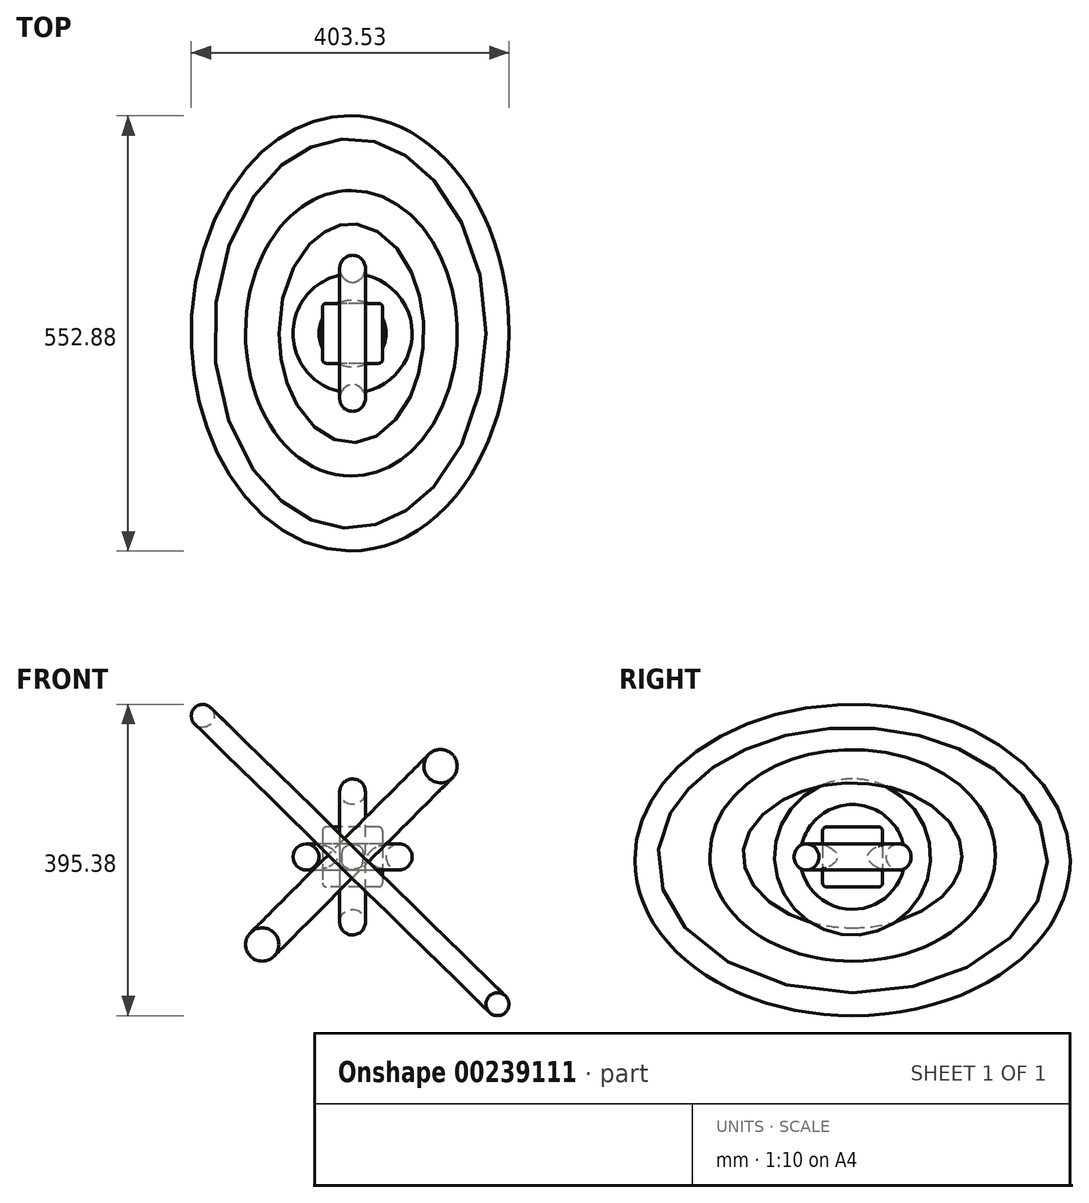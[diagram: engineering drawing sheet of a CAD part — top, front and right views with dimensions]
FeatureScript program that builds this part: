
annotation { "Feature Type Name" : "Feature", "Feature Type Description" : "" }
export const myFeature = defineFeature(function(context is Context, id is Id, definition is map)
    precondition{}
    {
        {
            var Q0;
            Q0=qCreatedBy(makeId("Front.planeOp"),FACE);
            var sketch = newSketch(context, id + "F0", { "sketchPlane" : qUnion([Q0])});
            skLineSegment(sketch, "E0.bottom", {"start": v(38.1, 38.1) * mm, "end": v(-38.1, 38.1) * mm});
            skLineSegment(sketch, "E0.top", {"start": v(38.1, -38.1) * mm, "end": v(-38.1, -38.1) * mm});
            skLineSegment(sketch, "E0.left", {"start": v(38.1, 38.1) * mm, "end": v(38.1, -38.1) * mm});
            skLineSegment(sketch, "E0.right", {"start": v(-38.1, 38.1) * mm, "end": v(-38.1, -38.1) * mm});
            skPoint(sketch, "E0.middle", {"position": v(0, 0) * mm});
            skSolve(sketch);
        }
        {
            var Q0;
            Q0 = qSketchRegion(id + "F0", true);
            extrude(context, id + "F1", {"entities" : qUnion([Q0]), "endBound" : BoundingType.SYMMETRIC, "depth" : 76.2 * mm});
        }
        {
            var Q0;
            Q0=makeQuery(id+"F1.opExtrude","CAP_EDGE",EDGE,{"disambiguationData":[OSD([sQuery(id+"F0.wireOp",EDGE,"E0.bottom")])],"isStart":true});
            var Q1;
            Q1=makeQuery(id+"F1.opExtrude","CAP_EDGE",EDGE,{"disambiguationData":[OSD([sQuery(id+"F0.wireOp",EDGE,"E0.top")])],"isStart":true});
            var Q2;
            Q2=makeQuery(id+"F1.opExtrude","CAP_EDGE",EDGE,{"disambiguationData":[OSD([sQuery(id+"F0.wireOp",EDGE,"E0.left")])],"isStart":true});
            var Q3;
            Q3=makeQuery(id+"F1.opExtrude","CAP_EDGE",EDGE,{"disambiguationData":[OSD([sQuery(id+"F0.wireOp",EDGE,"E0.right")])],"isStart":true});
            var Q4;
            Q4=makeQuery(id+"F1.opExtrude","CAP_EDGE",EDGE,{"disambiguationData":[OSD([sQuery(id+"F0.wireOp",EDGE,"E0.right")])],"isStart":false});
            var Q5;
            Q5=makeQuery(id+"F1.opExtrude","CAP_EDGE",EDGE,{"disambiguationData":[OSD([sQuery(id+"F0.wireOp",EDGE,"E0.bottom")])],"isStart":false});
            var Q6;
            Q6=makeQuery(id+"F1.opExtrude","CAP_EDGE",EDGE,{"disambiguationData":[OSD([sQuery(id+"F0.wireOp",EDGE,"E0.top")])],"isStart":false});
            var Q7;
            Q7=makeQuery(id+"F1.opExtrude","CAP_EDGE",EDGE,{"disambiguationData":[OSD([sQuery(id+"F0.wireOp",EDGE,"E0.left")])],"isStart":false});
            var Q8;
            Q8=makeQuery(id+"F1.opExtrude","SWEPT_EDGE",EDGE,{"disambiguationData":[OSD([sQuery(id+"F0.wireOp",EDGE,"E0.bottom"),sQuery(id+"F0.wireOp",EDGE,"E0.left")])]});
            var Q9;
            Q9=makeQuery(id+"F1.opExtrude","SWEPT_EDGE",EDGE,{"disambiguationData":[OSD([sQuery(id+"F0.wireOp",EDGE,"E0.bottom"),sQuery(id+"F0.wireOp",EDGE,"E0.right")])]});
            var Q10;
            Q10=makeQuery(id+"F1.opExtrude","SWEPT_EDGE",EDGE,{"disambiguationData":[OSD([sQuery(id+"F0.wireOp",EDGE,"E0.top"),sQuery(id+"F0.wireOp",EDGE,"E0.right")])]});
            var Q11;
            Q11=makeQuery(id+"F1.opExtrude","SWEPT_FACE",FACE,{"disambiguationData":[OSD([sQuery(id+"F0.wireOp",EDGE,"E0.top")])]});
            fillet(context, id + "F2", {"entities" : qUnion([Q0, Q1, Q2, Q3, Q4, Q5, Q6, Q7, Q8, Q9, Q10, Q11]), "radius" : 5.08 * mm, "tangentPropagation" : true, "allowEdgeOverflow" : false});
        }
        {
            var Q0;
            Q0=qCreatedBy(makeId("Right.planeOp"),FACE);
            var sketch = newSketch(context, id + "F3", { "sketchPlane" : qUnion([Q0])});
            skLineSegment(sketch, "E1", {"start": v(0, 18.36) * mm, "end": v(0, -15.93) * mm});
            skCircle(sketch, "E2", {"center": v(59.16, 0) * mm, "radius": 16.55 * mm});
            skSolve(sketch);
        }
        {
            var Q0;
            Q0 = qSketchRegion(id + "F3", true);
            var Q1;
            Q1=sQuery(id+"F3.wireOp",EDGE,"E1");
            revolve(context, id + "F4", {"operationType" : NewBodyOperationType.ADD, "entities" : qUnion([Q0]), "axis" : qUnion([Q1]), "revolveType" : RevolveType.FULL});
        }
        {
            var Q0;
            Q0=qCreatedBy(makeId("Front.planeOp"),FACE);
            var sketch = newSketch(context, id + "F5", { "sketchPlane" : qUnion([Q0])});
            skLineSegment(sketch, "E3", {"start": v(8.95, 0) * mm, "end": v(-13.2, 0) * mm});
            skCircle(sketch, "E4", {"center": v(0, 82.83) * mm, "radius": 16.28 * mm});
            skSolve(sketch);
        }
        {
            var Q0;
            Q0 = qSketchRegion(id + "F5", true);
            var Q1;
            Q1=sQuery(id+"F5.wireOp",EDGE,"E3");
            revolve(context, id + "F6", {"operationType" : NewBodyOperationType.ADD, "entities" : qUnion([Q0]), "axis" : qUnion([Q1]), "revolveType" : RevolveType.FULL});
        }
        {
            var Q0;
            Q0=qCreatedBy(makeId("Front.planeOp"),FACE);
            var sketch = newSketch(context, id + "F7", { "sketchPlane" : qUnion([Q0])});
            skLineSegment(sketch, "E5", {"start": v(50.12, -49.58) * mm, "end": v(-43.4, 43.95) * mm});
            skCircle(sketch, "E6", {"center": v(111.74, 115.3) * mm, "radius": 21.2 * mm});
            skSolve(sketch);
        }
        {
            var Q0;
            Q0 = qSketchRegion(id + "F7", true);
            var Q1;
            Q1=sQuery(id+"F7.wireOp",EDGE,"E5");
            revolve(context, id + "F8", {"entities" : qUnion([Q0]), "axis" : qUnion([Q1]), "revolveType" : RevolveType.FULL});
        }
        {
            var Q0;
            Q0=qCreatedBy(makeId("Front.planeOp"),FACE);
            var sketch = newSketch(context, id + "F9", { "sketchPlane" : qUnion([Q0])});
            skLineSegment(sketch, "E7", {"start": v(22.7, 22.43) * mm, "end": v(-25.95, -27.3) * mm});
            skCircle(sketch, "E8", {"center": v(-190.29, 179.2) * mm, "radius": 14.56 * mm});
            skSolve(sketch);
        }
        {
            var Q0;
            Q0 = qSketchRegion(id + "F9", true);
            var Q1;
            Q1=sQuery(id+"F9.wireOp",EDGE,"E7");
            revolve(context, id + "F10", {"entities" : qUnion([Q0]), "axis" : qUnion([Q1]), "revolveType" : RevolveType.FULL});
        }
    });
